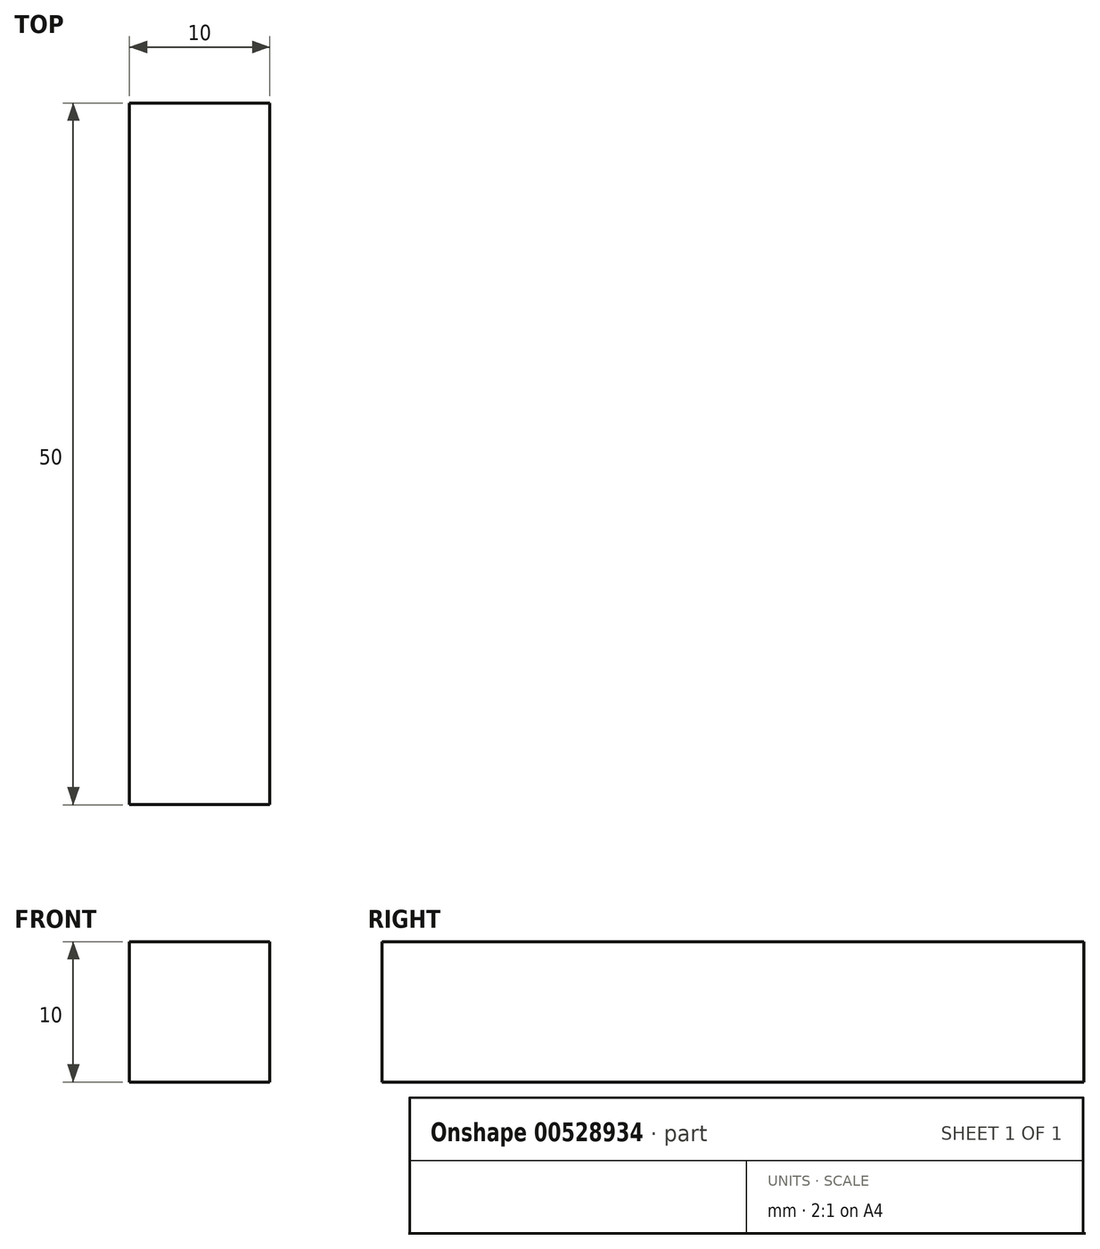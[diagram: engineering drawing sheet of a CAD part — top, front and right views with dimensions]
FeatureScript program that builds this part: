
annotation { "Feature Type Name" : "Feature", "Feature Type Description" : "" }
export const myFeature = defineFeature(function(context is Context, id is Id, definition is map)
    precondition{}
    {
        {
            var Q0;
            Q0=qCreatedBy(makeId("Top.planeOp"),FACE);
            var sketch = newSketch(context, id + "F0", { "sketchPlane" : qUnion([Q0])});
            skLineSegment(sketch, "E0.bottom", {"start": v(-65.76, 7.5) * mm, "end": v(-75.76, 7.5) * mm});
            skLineSegment(sketch, "E0.top", {"start": v(-65.76, 57.5) * mm, "end": v(-75.76, 57.5) * mm});
            skLineSegment(sketch, "E0.left", {"start": v(-65.76, 7.5) * mm, "end": v(-65.76, 57.5) * mm});
            skLineSegment(sketch, "E0.right", {"start": v(-75.76, 7.5) * mm, "end": v(-75.76, 57.5) * mm});
            skPoint(sketch, "E0.middle", {"position": v(-70.76, 32.5) * mm});
            skSolve(sketch);
        }
        {
            var Q0;
            Q0=makeQuery(id+"F0.imprint","IMPRINT",FACE,{"disambiguationData":[TD([[makeQuery(id+"F0.imprint","IMPRINT",EDGE,{"derivedFrom":sQuery(id+"F0.wireOp",EDGE,"E0.bottom")}),-1.0]])]});
            extrude(context, id + "F1", {"entities" : qUnion([Q0]), "depth" : 10 * mm, "offsetDistance" : 25 * mm});
        }
    });
